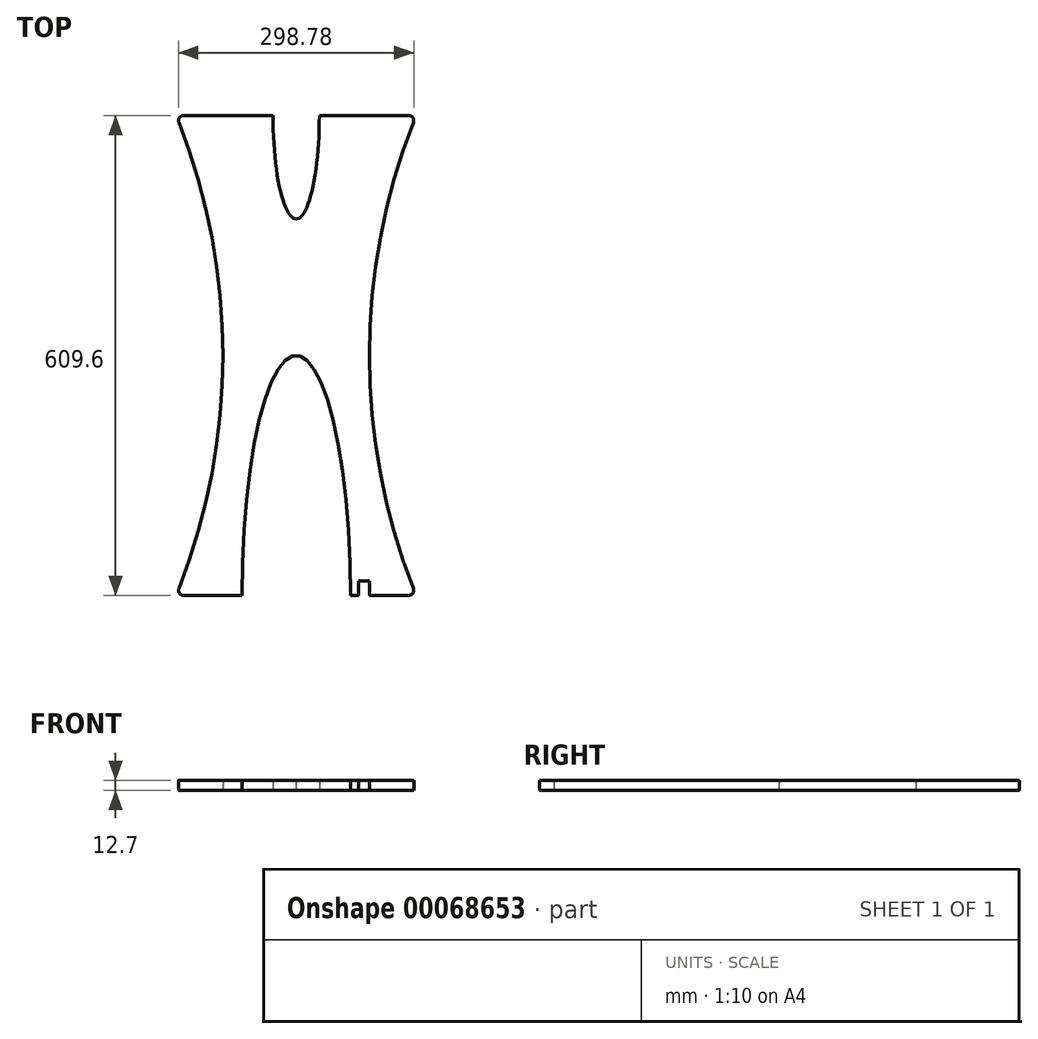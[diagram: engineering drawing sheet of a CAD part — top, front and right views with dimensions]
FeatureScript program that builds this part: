
annotation { "Feature Type Name" : "Feature", "Feature Type Description" : "" }
export const myFeature = defineFeature(function(context is Context, id is Id, definition is map)
    precondition{}
    {
        {
            var Q0;
            Q0=qCreatedBy(makeId("Top.planeOp"),FACE);
            var sketch = newSketch(context, id + "F0", { "sketchPlane" : qUnion([Q0])});
            skLineSegment(sketch, "E0", {"start": v(68.8, 0) * mm, "end": v(78.92, 0) * mm});
            skEllipticalArc(sketch, "E1", {});
            skLineSegment(sketch, "E2", {"start": v(0, 0) * mm, "end": v(0, 667.62) * mm, "construction": true});
            skArc(sketch, "E3", {"start": v(148.95, 600.94) * mm, "mid": v(93.09, 304.8) * mm, "end": v(148.95, 8.66) * mm});
            skEllipticalArc(sketch, "E4", {});
            skPoint(sketch, "E5.visualSharp", {"position": v(152.4, 0) * mm});
            skArc(sketch, "E5.filletArc", {"start": v(143.04, 0) * mm, "mid": v(148.28, 2.77) * mm, "end": v(148.95, 8.66) * mm});
            skPoint(sketch, "E6.visualSharp", {"position": v(152.4, 609.6) * mm});
            skArc(sketch, "E6.filletArc", {"start": v(148.95, 600.94) * mm, "mid": v(148.28, 606.83) * mm, "end": v(143.04, 609.6) * mm});
            skArc(sketch, "E7.MirrorCS", {"start": v(-143.04, 0) * mm, "mid": v(-148.28, 2.77) * mm, "end": v(-148.95, 8.66) * mm});
            skArc(sketch, "E8.MirrorCS", {"start": v(-148.95, 600.94) * mm, "mid": v(-148.28, 606.83) * mm, "end": v(-143.04, 609.6) * mm});
            skEllipticalArc(sketch, "E9.MirrorCS", {});
            skEllipticalArc(sketch, "E10.MirrorCS", {});
            skLineSegment(sketch, "E11.MirrorCS", {"start": v(-68.8, 0) * mm, "end": v(-143.04, 0) * mm});
            skArc(sketch, "E12.MirrorCS", {"start": v(-148.95, 600.94) * mm, "mid": v(-93.09, 304.8) * mm, "end": v(-148.95, 8.66) * mm});
            skPoint(sketch, "E13.MirrorP", {"position": v(-152.4, 609.6) * mm});
            skPoint(sketch, "E14.MirrorP", {"position": v(-152.4, 0) * mm});
            skLineSegment(sketch, "E15", {"start": v(-29.43, 609.6) * mm, "end": v(-143.04, 609.6) * mm});
            skLineSegment(sketch, "E16", {"start": v(143.04, 609.6) * mm, "end": v(29.43, 609.6) * mm});
            skLineSegment(sketch, "E17.top", {"start": v(78.92, 18.14) * mm, "end": v(93.4, 18.14) * mm});
            skLineSegment(sketch, "E17.left", {"start": v(78.92, 0) * mm, "end": v(78.92, 18.14) * mm});
            skLineSegment(sketch, "E17.right", {"start": v(93.4, 0) * mm, "end": v(93.4, 18.14) * mm});
            skLineSegment(sketch, "E18.trimOffspring", {"start": v(93.4, 0) * mm, "end": v(143.04, 0) * mm});
            const initialGuessF0  = {"E1": [0, 0, 0, 1, 0.3048, 0.06880619994088923, 4.71238898038469, 0], "E4": [0, 0.6096302270889282, 0.999999472625248, -0.0010270098470219235, 0.029432131557300123, 0.13147899189327653, 4.7169768011112065, 6.283185307179586], "E9.MirrorCS": [0, 0, 0, 1, 0.3048, 0.06880619994088923, 0, 1.5707963267948966], "E10.MirrorCS": [0, 0.6096302270889282, -0.999999472625248, -0.0010270098470219235, 0.029432131557300123, 0.13147899189327653, 6.283185307179586, 1.5662085060683797]};
            skSetInitialGuess(sketch, initialGuessF0);
            skSolve(sketch);
        }
        {
            var Q0;
            Q0=qSketchRegion(id+"F0",true);
            extrude(context, id + "F1", {"entities" : qUnion([Q0]), "depth" : 12.7 * mm});
        }
    });
